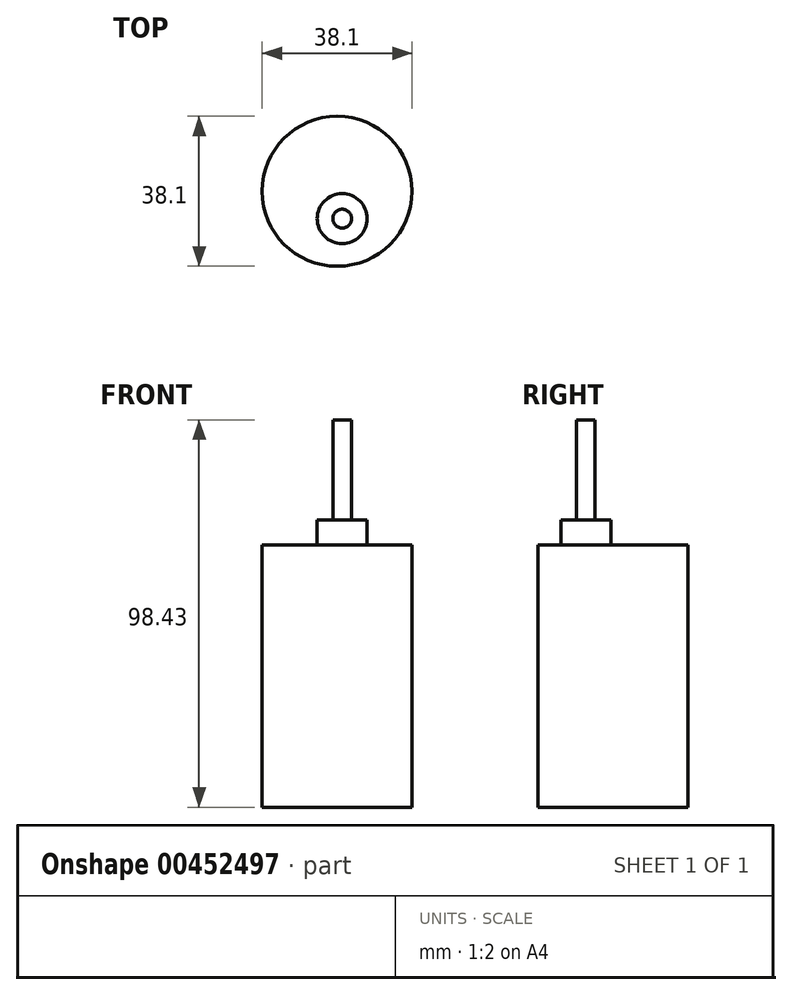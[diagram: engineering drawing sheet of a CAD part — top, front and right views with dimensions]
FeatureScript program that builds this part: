
annotation { "Feature Type Name" : "Feature", "Feature Type Description" : "" }
export const myFeature = defineFeature(function(context is Context, id is Id, definition is map)
    precondition{}
    {
        {
            var Q0;
            Q0=qCreatedBy(makeId("Top.planeOp"),FACE);
            var sketch = newSketch(context, id + "F0", { "sketchPlane" : qUnion([Q0])});
            skCircle(sketch, "E0", {"center": v(0, 0) * mm, "radius": 19.05 * mm});
            skSolve(sketch);
        }
        {
            var Q0;
            Q0=qSketchRegion(id+"F0",true);
            extrude(context, id + "F1", {"entities" : qUnion([Q0]), "depth" : 66.67 * mm});
        }
        {
            var Q0;
            Q0=makeQuery(id+"F1.opExtrude","CAP_FACE",FACE,{"disambiguationData":[OSD([sQuery(id+"F0.wireOp",EDGE,"E0")])],"isStart":false});
            var sketch = newSketch(context, id + "F2", { "sketchPlane" : qUnion([Q0])});
            skLineSegment(sketch, "E1", {"start": v(-4.72, 18.45) * mm, "end": v(4.05, -18.61) * mm});
            skPoint(sketch, "E2", {"position": v(1.29, -6.95) * mm});
            skCircle(sketch, "E3", {"center": v(1.29, -6.95) * mm, "radius": 6.35 * mm});
            skSolve(sketch);
        }
        {
            var Q0;
            Q0=qSketchRegion(id+"F2",true);
            extrude(context, id + "F3", {"entities" : qUnion([Q0]), "operationType" : NewBodyOperationType.ADD, "depth" : 6.35 * mm});
        }
        {
            var Q0;
            Q0=makeQuery(id+"F3.opExtrude","CAP_FACE",FACE,{"disambiguationData":[OSD([sQuery(id+"F2.wireOp",EDGE,"E3")])],"isStart":false});
            var sketch = newSketch(context, id + "F4", { "sketchPlane" : qUnion([Q0])});
            skPoint(sketch, "E4", {"position": v(1.29, -6.95) * mm});
            skCircle(sketch, "E5", {"center": v(1.29, -6.95) * mm, "radius": 2.38 * mm});
            skSolve(sketch);
        }
        {
            var Q0;
            Q0=qSketchRegion(id+"F4",true);
            extrude(context, id + "F5", {"entities" : qUnion([Q0]), "operationType" : NewBodyOperationType.ADD, "depth" : 25.4 * mm});
        }
    });
